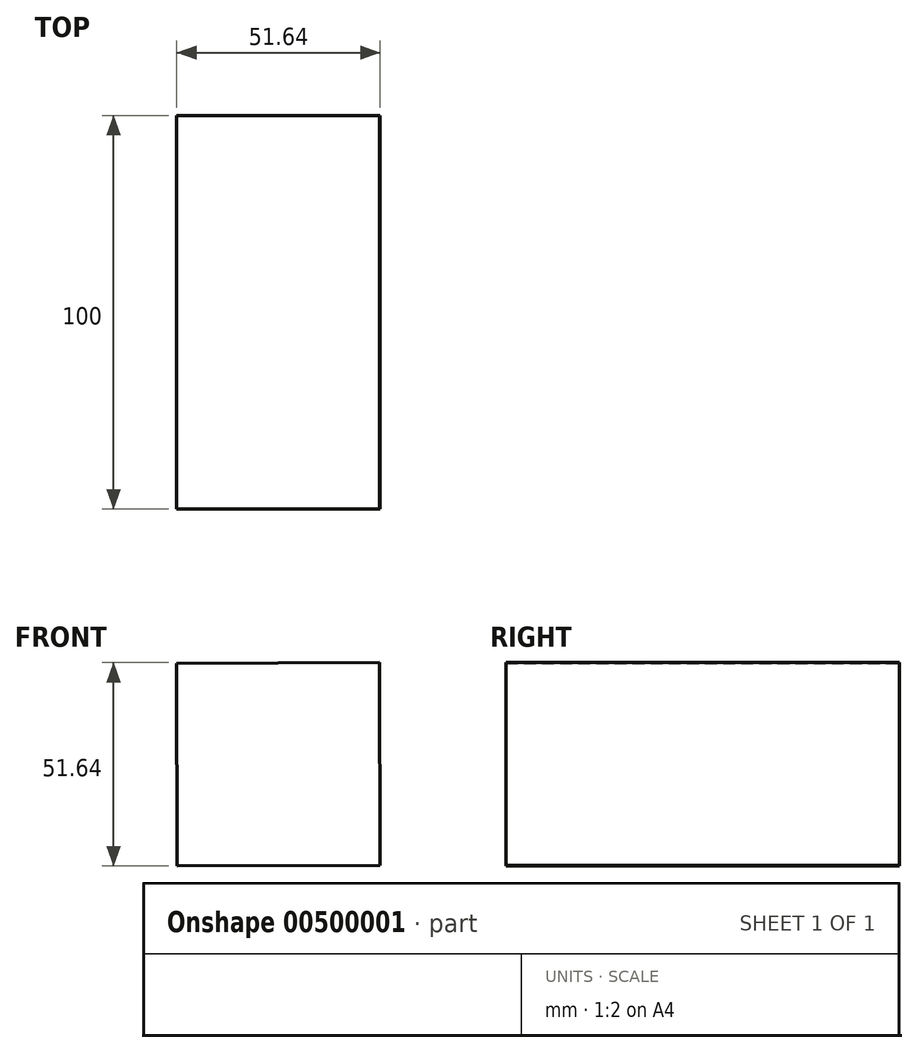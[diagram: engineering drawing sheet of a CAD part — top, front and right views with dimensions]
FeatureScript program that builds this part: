
annotation { "Feature Type Name" : "Feature", "Feature Type Description" : "" }
export const myFeature = defineFeature(function(context is Context, id is Id, definition is map)
    precondition{}
    {
        {
            var Q0;
            Q0=qCreatedBy(makeId("Front.planeOp"),FACE);
            var sketch = newSketch(context, id + "F0", { "sketchPlane" : qUnion([Q0])});
            skCircle(sketch, "E0.cCircle", {"center": v(0, 0) * mm, "radius": 36.41 * mm, "construction": true});
            skLineSegment(sketch, "E0.0", {"start": v(-25.82, 25.68) * mm, "end": v(25.68, 25.82) * mm});
            skLineSegment(sketch, "E0.1", {"start": v(25.68, 25.82) * mm, "end": v(25.82, -25.68) * mm});
            skLineSegment(sketch, "E0.2", {"start": v(25.82, -25.68) * mm, "end": v(-25.68, -25.82) * mm});
            skLineSegment(sketch, "E0.3", {"start": v(-25.68, -25.82) * mm, "end": v(-25.82, 25.68) * mm});
            skSolve(sketch);
        }
        {
            var Q0;
            Q0 = qSketchRegion(id + "F0", true);
            extrude(context, id + "F1", {"entities" : qUnion([Q0]), "endBound" : BoundingType.SYMMETRIC, "depth" : 100 * mm});
        }
    });
